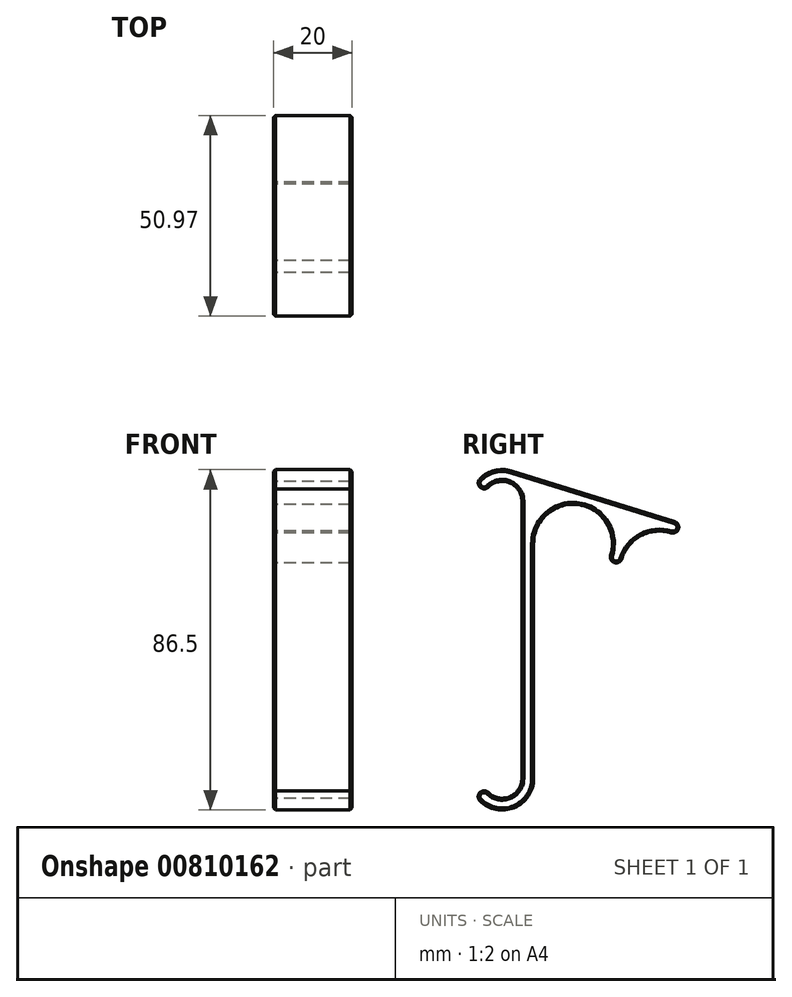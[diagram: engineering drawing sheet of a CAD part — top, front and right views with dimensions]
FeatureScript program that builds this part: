
annotation { "Feature Type Name" : "Feature", "Feature Type Description" : "" }
export const myFeature = defineFeature(function(context is Context, id is Id, definition is map)
    precondition{}
    {
        {
            var Q0;
            Q0=qCreatedBy(makeId("Right.planeOp"),FACE);
            var sketch = newSketch(context, id + "F0", { "sketchPlane" : qUnion([Q0])});
            skCircle(sketch, "E0", {"center": v(0, 0) * mm, "radius": 5 * mm});
            skCircle(sketch, "E1", {"center": v(0, 0) * mm, "radius": 8 * mm});
            skLineSegment(sketch, "E2", {"start": v(8, 0) * mm, "end": v(8, -70.5) * mm});
            skLineSegment(sketch, "E3", {"start": v(5, 0) * mm, "end": v(5, -70.5) * mm});
            skCircle(sketch, "E4", {"center": v(0, -70.5) * mm, "radius": 5 * mm});
            skCircle(sketch, "E5", {"center": v(0, -70.5) * mm, "radius": 8 * mm});
            skCircle(sketch, "E6", {"center": v(-4.6, 4.6) * mm, "radius": 1.5 * mm});
            skCircle(sketch, "E7", {"center": v(-4.6, -75.1) * mm, "radius": 1.5 * mm});
            skLineSegment(sketch, "E8", {"start": v(0, -70.5) * mm, "end": v(-6.87, -77.37) * mm, "construction": true});
            skLineSegment(sketch, "E9", {"start": v(0, 0) * mm, "end": v(-5.8, 5.8) * mm, "construction": true});
            skCircle(sketch, "E10", {"center": v(18, -10.82) * mm, "radius": 13 * mm});
            skLineSegment(sketch, "E11", {"start": v(2.37, 7.64) * mm, "end": v(21.85, 1.6) * mm});
            skCircle(sketch, "E12", {"center": v(18, -10.82) * mm, "radius": 10 * mm});
            skCircle(sketch, "E13", {"center": v(28.98, -14.22) * mm, "radius": 1.5 * mm});
            skCircle(sketch, "E14", {"center": v(39.97, -17.63) * mm, "radius": 10 * mm});
            skLineSegment(sketch, "E15", {"start": v(21.85, 1.6) * mm, "end": v(65.9, -12.06) * mm});
            skCircle(sketch, "E16", {"center": v(43.37, -6.64) * mm, "radius": 1.5 * mm});
            skLineSegment(sketch, "E17", {"start": v(39.97, -17.63) * mm, "end": v(43.82, -5.21) * mm, "construction": true});
            skSolve(sketch);
        }
        {
            var Q0;
            {var subQ0=sQuery(id+"F0.wireOp",EDGE,"E2");Q0=makeQuery(id+"F0.imprint","IMPRINT",FACE,{"disambiguationData":[TD([[makeQuery(id+"F0.imprint","IMPRINT",EDGE,{"derivedFrom":subQ0}),-1.0]])]});}
            var Q1;
            {var subQ0=sQuery(id+"F0.wireOp",EDGE,"E3");var subQ1=sQuery(id+"F0.wireOp",EDGE,"E0");var subQ2=makeQuery(id+"F0.imprint","INTERSECT",VERTEX,{"derivedFrom":[subQ1,subQ0]});Q1=makeQuery(id+"F0.imprint","IMPRINT",FACE,{"disambiguationData":[TD([[makeQuery(id+"F0.imprint","IMPRINT",EDGE,{"disambiguationData":[TD([[subQ2,-1.0]])],"derivedFrom":subQ1}),-1.0]])]});}
            var Q2;
            {var subQ0=sQuery(id+"F0.wireOp",EDGE,"E6");var subQ1=makeQuery(id+"F0.imprint","INTERSECT",VERTEX,{"derivedFrom":[sQuery(id+"F0.wireOp",EDGE,"E1"),subQ0]});Q2=makeQuery(id+"F0.imprint","IMPRINT",FACE,{"disambiguationData":[TD([[makeQuery(id+"F0.imprint","IMPRINT",EDGE,{"disambiguationData":[TD([[subQ1,-1.0]])],"derivedFrom":subQ0}),1.0]])]});}
            var Q3;
            {var subQ2=sQuery(id+"F0.wireOp",EDGE,"E3");var subQ4=sQuery(id+"F0.wireOp",EDGE,"E4");var subQ5=makeQuery(id+"F0.imprint","INTERSECT",VERTEX,{"derivedFrom":[subQ2,subQ4]});Q3=makeQuery(id+"F0.imprint","IMPRINT",FACE,{"disambiguationData":[TD([[makeQuery(id+"F0.imprint","IMPRINT",EDGE,{"disambiguationData":[TD([[subQ5,1.0]])],"derivedFrom":subQ2}),1.0]])]});}
            var Q4;
            {var subQ0=sQuery(id+"F0.wireOp",EDGE,"E7");var subQ1=makeQuery(id+"F0.imprint","INTERSECT",VERTEX,{"derivedFrom":[sQuery(id+"F0.wireOp",EDGE,"E5"),subQ0]});Q4=makeQuery(id+"F0.imprint","IMPRINT",FACE,{"disambiguationData":[TD([[makeQuery(id+"F0.imprint","IMPRINT",EDGE,{"disambiguationData":[TD([[subQ1,1.0]])],"derivedFrom":subQ0}),1.0]])]});}
            var Q5;
            {var subQ0=sQuery(id+"F0.wireOp",EDGE,"E3");var subQ1=sQuery(id+"F0.wireOp",EDGE,"E1");var subQ2=makeQuery(id+"F0.imprint","INTERSECT",VERTEX,{"derivedFrom":[subQ1,subQ0]});Q5=makeQuery(id+"F0.imprint","IMPRINT",FACE,{"disambiguationData":[TD([[makeQuery(id+"F0.imprint","IMPRINT",EDGE,{"disambiguationData":[TD([[subQ2,-1.0]])],"derivedFrom":subQ1}),-1.0]])]});}
            var Q6;
            {var subQ1=sQuery(id+"F0.wireOp",EDGE,"E2");var subQ5=sQuery(id+"F0.wireOp",EDGE,"E10");var subQ7=makeQuery(id+"F0.imprint","INTERSECT",VERTEX,{"disambiguationData":[OD(1.0)],"derivedFrom":[subQ1,subQ5]});Q6=makeQuery(id+"F0.imprint","IMPRINT",FACE,{"disambiguationData":[TD([[makeQuery(id+"F0.imprint","IMPRINT",EDGE,{"disambiguationData":[TD([[subQ7,-1.0]])],"derivedFrom":subQ1}),1.0]])]});}
            var Q7;
            {var subQ0=sQuery(id+"F0.wireOp",EDGE,"E13");var subQ1=makeQuery(id+"F0.imprint","INTERSECT",VERTEX,{"derivedFrom":[sQuery(id+"F0.wireOp",EDGE,"E10"),subQ0]});Q7=makeQuery(id+"F0.imprint","IMPRINT",FACE,{"disambiguationData":[TD([[makeQuery(id+"F0.imprint","IMPRINT",EDGE,{"disambiguationData":[TD([[subQ1,1.0]])],"derivedFrom":subQ0}),1.0]])]});}
            var Q8;
            {var subQ0=sQuery(id+"F0.wireOp",EDGE,"E2");var subQ1=sQuery(id+"F0.wireOp",EDGE,"E1");var subQ2=makeQuery(id+"F0.imprint","INTERSECT",VERTEX,{"derivedFrom":[subQ1,subQ0]});Q8=makeQuery(id+"F0.imprint","IMPRINT",FACE,{"disambiguationData":[TD([[makeQuery(id+"F0.imprint","IMPRINT",EDGE,{"disambiguationData":[TD([[subQ2,1.0]])],"derivedFrom":subQ1}),-1.0]])]});}
            var Q9;
            {var subQ0=sQuery(id+"F0.wireOp",EDGE,"E5");var subQ1=sQuery(id+"F0.wireOp",EDGE,"E2");var subQ2=makeQuery(id+"F0.imprint","INTERSECT",VERTEX,{"derivedFrom":[subQ1,subQ0]});Q9=makeQuery(id+"F0.imprint","IMPRINT",FACE,{"disambiguationData":[TD([[makeQuery(id+"F0.imprint","IMPRINT",EDGE,{"disambiguationData":[TD([[subQ2,1.0]])],"derivedFrom":subQ1}),-1.0]])]});}
            var Q10;
            {var subQ3=sQuery(id+"F0.wireOp",EDGE,"E11");Q10=makeQuery(id+"F0.imprint","IMPRINT",FACE,{"disambiguationData":[TD([[makeQuery(id+"F0.imprint","IMPRINT",EDGE,{"derivedFrom":subQ3}),-1.0]])]});}
            var Q11;
            {var subQ0=sQuery(id+"F0.wireOp",EDGE,"E15");var subQ5=sQuery(id+"F0.wireOp",EDGE,"E16");var subQ7=makeQuery(id+"F0.imprint","INTERSECT",VERTEX,{"derivedFrom":[subQ0,subQ5]});Q11=makeQuery(id+"F0.imprint","IMPRINT",FACE,{"disambiguationData":[TD([[makeQuery(id+"F0.imprint","IMPRINT",EDGE,{"disambiguationData":[TD([[subQ7,-1.0]])],"derivedFrom":subQ5}),-1.0]])]});}
            var Q12;
            {var subQ0=sQuery(id+"F0.wireOp",EDGE,"E16");var subQ1=makeQuery(id+"F0.imprint","INTERSECT",VERTEX,{"derivedFrom":[sQuery(id+"F0.wireOp",EDGE,"E15"),subQ0]});Q12=makeQuery(id+"F0.imprint","IMPRINT",FACE,{"disambiguationData":[TD([[makeQuery(id+"F0.imprint","IMPRINT",EDGE,{"disambiguationData":[TD([[subQ1,-1.0]])],"derivedFrom":subQ0}),1.0]])]});}
            extrude(context, id + "F1", {"entities" : qUnion([Q0, Q1, Q2, Q3, Q4, Q5, Q6, Q7, Q8, Q9, Q10, Q11, Q12]), "depth" : 20 * mm, "offsetDistance" : 25 * mm});
        }
        {
            var Q0;
            Q0=makeQuery(id+"F1.opExtrude","CAP_FACE",FACE,{"disambiguationData":[OSD([sQuery(id+"F0.wireOp",EDGE,"E0"),sQuery(id+"F0.wireOp",EDGE,"E1"),sQuery(id+"F0.wireOp",EDGE,"E2"),sQuery(id+"F0.wireOp",EDGE,"E3"),sQuery(id+"F0.wireOp",EDGE,"E4"),sQuery(id+"F0.wireOp",EDGE,"E5"),sQuery(id+"F0.wireOp",EDGE,"E6"),sQuery(id+"F0.wireOp",EDGE,"E7"),sQuery(id+"F0.wireOp",EDGE,"E10"),sQuery(id+"F0.wireOp",EDGE,"E11"),sQuery(id+"F0.wireOp",EDGE,"E12"),sQuery(id+"F0.wireOp",EDGE,"E13")])],"isStart":false});
            var Q1;
            Q1=makeQuery(id+"F1.opExtrude","CAP_FACE",FACE,{"disambiguationData":[OSD([sQuery(id+"F0.wireOp",EDGE,"E0"),sQuery(id+"F0.wireOp",EDGE,"E1"),sQuery(id+"F0.wireOp",EDGE,"E2"),sQuery(id+"F0.wireOp",EDGE,"E3"),sQuery(id+"F0.wireOp",EDGE,"E4"),sQuery(id+"F0.wireOp",EDGE,"E5"),sQuery(id+"F0.wireOp",EDGE,"E6"),sQuery(id+"F0.wireOp",EDGE,"E7"),sQuery(id+"F0.wireOp",EDGE,"E10"),sQuery(id+"F0.wireOp",EDGE,"E11"),sQuery(id+"F0.wireOp",EDGE,"E12"),sQuery(id+"F0.wireOp",EDGE,"E13")])],"isStart":true});
            chamfer(context, id + "F2", {"entities" : qUnion([Q0, Q1]), "width" : 0.5 * mm, "tangentPropagation" : true});
        }
    });
